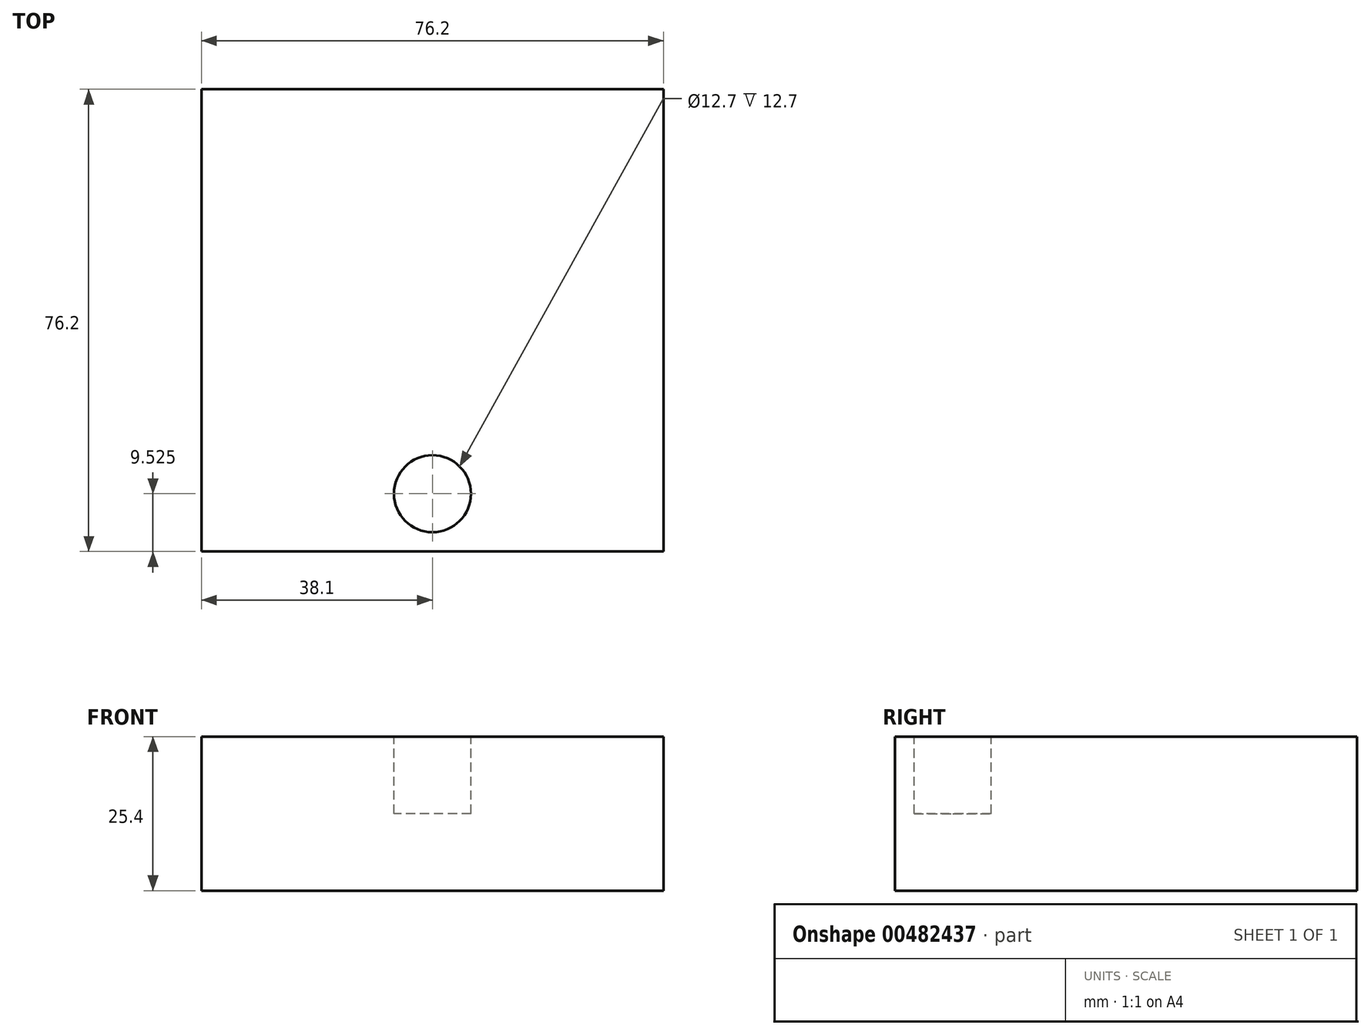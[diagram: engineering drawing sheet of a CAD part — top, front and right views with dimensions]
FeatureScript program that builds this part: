
annotation { "Feature Type Name" : "Feature", "Feature Type Description" : "" }
export const myFeature = defineFeature(function(context is Context, id is Id, definition is map)
    precondition{}
    {
        {
            var Q0;
            Q0=qCreatedBy(makeId("Top.planeOp"),FACE);
            var sketch = newSketch(context, id + "F0", { "sketchPlane" : qUnion([Q0])});
            skLineSegment(sketch, "E0.bottom", {"start": v(-38.1, 38.1) * mm, "end": v(38.1, 38.1) * mm});
            skLineSegment(sketch, "E0.top", {"start": v(-38.1, -38.1) * mm, "end": v(38.1, -38.1) * mm});
            skLineSegment(sketch, "E0.left", {"start": v(-38.1, 38.1) * mm, "end": v(-38.1, -38.1) * mm});
            skLineSegment(sketch, "E0.right", {"start": v(38.1, 38.1) * mm, "end": v(38.1, -38.1) * mm});
            skPoint(sketch, "E0.middle", {"position": v(0, 0) * mm});
            skSolve(sketch);
        }
        {
            var Q0;
            Q0=makeQuery(id+"F0.imprint","IMPRINT",FACE,{"disambiguationData":[TD([[makeQuery(id+"F0.imprint","IMPRINT",EDGE,{"derivedFrom":sQuery(id+"F0.wireOp",EDGE,"E0.bottom")}),-1.0]])]});
            extrude(context, id + "F1", {"entities" : qUnion([Q0]), "depth" : 25.4 * mm});
        }
        {
            var Q0;
            Q0=makeQuery(id+"F1.opExtrude","CAP_FACE",FACE,{"disambiguationData":[OSD([sQuery(id+"F0.wireOp",EDGE,"E0.bottom"),sQuery(id+"F0.wireOp",EDGE,"E0.top"),sQuery(id+"F0.wireOp",EDGE,"E0.left"),sQuery(id+"F0.wireOp",EDGE,"E0.right")])],"isStart":false});
            var sketch = newSketch(context, id + "F2", { "sketchPlane" : qUnion([Q0])});
            skCircle(sketch, "E1", {"center": v(0, 0) * mm, "radius": 28.58 * mm, "construction": true});
            skCircle(sketch, "E2", {"center": v(0, -28.58) * mm, "radius": 6.35 * mm});
            skSolve(sketch);
        }
        {
            var Q0;
            Q0 = qSketchRegion(id + "F2", true);
            extrude(context, id + "F3", {"entities" : qUnion([Q0]), "operationType" : NewBodyOperationType.REMOVE, "oppositeDirection" : true, "depth" : 12.7 * mm});
        }
    });
